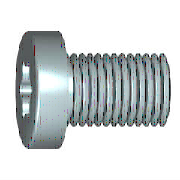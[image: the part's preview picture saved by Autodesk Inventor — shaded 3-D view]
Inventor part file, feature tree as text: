
AUTODESK INVENTOR PART (.ipt)
format: ipt  version: 2021 (Build 250183000, 183)  size: 244,224 bytes
history: native  units: mm (DEFAULTED — no unit token found)
features: other x2, sketch x1, extrude x1, plane x1
ambient origin geometry x7: Origin, YZ Plane, XY Plane, X Axis, Y Axis, Z Axis, Center Point
bodies: Solid1 (feature_tree), Body (feature_tree)
feature tree (5):
  sketch  "Sketch1"  dims[d1=28.0mm d2=1.2269mm d3=9.0mm d4=4.0mm d5=60.0deg d6=14.0mm d7=12.917mm d8=11.259mm d9=21.0mm d10=90.0deg d11=10.0mm d12=0.0mm d13=28.0mm d14=0.0mm d15=1.2269mm d16=1.227mm d17=0.9mm d19=0.0mm d20=30.0mm d30=45.0deg d33=0.0mm d34=0.45mm d35=0.872665mm d36=90.0deg d37=0.0mm d38=7.945mm d39=30.0deg d40=60.0deg d42=0.769mm d43=-5.235988mm]
  extrude  "Slot"  Depth=0.769mm
  other  "Taper"
  other  "Work Axis1"
  plane  "Work Plane1"
